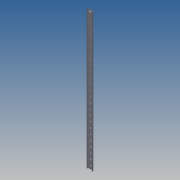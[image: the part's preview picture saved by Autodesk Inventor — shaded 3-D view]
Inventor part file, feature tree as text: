
AUTODESK INVENTOR PART (.ipt)
format: ipt  version: 2011 (Build 150239000, 239)  size: 275,968 bytes
history: native  units: mm
features: extrude x6, fillet x6, sketch x6
ambient origin geometry x8: Origin, YZ Plane, XZ Plane, XY Plane, X Axis, Y Axis, Z Axis, Center Point
feature tree (18):
  extrude  "Extrusion10"  Depth=510.0mm TaperAngle=0.0deg
  extrude  "Extrusion11"  Depth=1.0mm
  extrude  "Extrusion12"  Depth=5.0mm
  fillet  "Fillet12"  Radius=6.799998mm
  fillet  "Fillet13"  Radius=5.0mm
  fillet  "Fillet14"  Radius=6.799998mm
  fillet  "Fillet15"  Radius=4.5mm
  fillet  "Fillet16"  Radius=0.3mm
  fillet  "Fillet17"  Radius=0.3mm
  extrude  "Extrusion13"  Depth=0.1mm
  extrude  "Extrusion14"  Depth=1.0mm
  extrude  "Extrusion15"  Depth=20.0mm
  sketch  "Sketch1"  dims[d105=0.1mm d106=510.0mm d107=0.0mm]
  sketch  "Sketch12"  dims[d108=5.3mm d109=1.0mm]
  sketch  "Sketch13"  dims[d110=0.3mm d111=0.0mm d112=5.0mm d113=6.799998mm d115=5.0mm d116=6.799998mm d117=4.5mm d118=0.0mm d119=0.3mm d120=0.3mm]
  sketch  "Sketch14"  dims[d121=0.1mm d122=0.1mm]
  sketch  "Sketch15"  dims[d123=1.0mm d124=1.0mm]
  sketch  "Sketch16"  dims[d137=20.0mm d138=20.0mm d143=12.4mm d144=20.0mm d145=20.0mm d146=20.0mm d147=20.0mm d148=20.0mm d149=20.0mm d150=9.299998mm d151=9.299998mm d152=9.299998mm d153=9.299998mm d154=9.299998mm d155=9.299998mm d156=9.3mm d157=9.3mm d158=9.3mm d159=9.3mm d160=9.3mm d161=9.3mm d162=9.3mm d163=9.3mm d164=9.3mm d165=20.0mm d166=20.0mm d167=20.0mm d168=20.0mm d169=20.0mm d170=20.0mm d171=20.0mm d172=20.0mm d173=20.0mm d174=20.0mm d175=20.0mm d176=20.0mm d177=9.3mm d178=9.300002mm d179=9.3mm d180=9.3mm d181=20.0mm d182=20.0mm d183=9.3mm d184=20.0mm d185=2.0mm d186=0.0mm d193=1.0mm d194=0.0mm d196=5.0mm d198=100.0mm d199=100.0mm d200=100.0mm d201=100.0mm d202=55.0mm d203=1.7mm d204=1.7mm d205=1.7mm d206=1.7mm d207=1.7mm d208=1.7mm d209=1.0mm d210=0.0mm]
